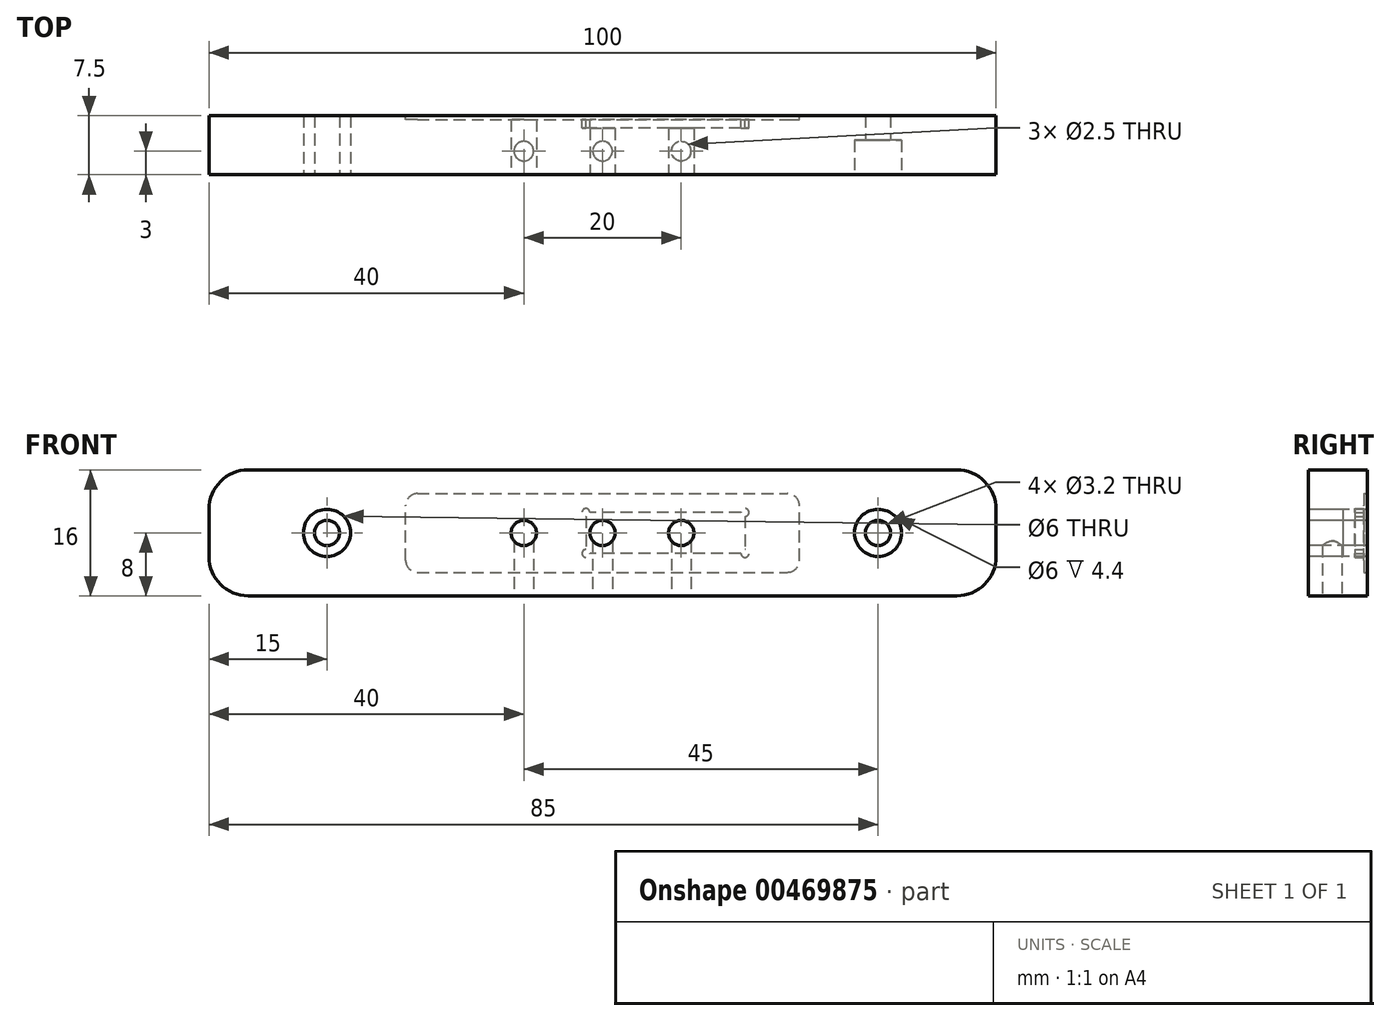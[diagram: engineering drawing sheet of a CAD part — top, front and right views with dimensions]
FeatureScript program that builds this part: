
annotation { "Feature Type Name" : "Feature", "Feature Type Description" : "" }
export const myFeature = defineFeature(function(context is Context, id is Id, definition is map)
    precondition{}
    {
        {
            var Q0;
            Q0=qCreatedBy(makeId("Front.planeOp"),FACE);
            var sketch = newSketch(context, id + "F0", { "sketchPlane" : qUnion([Q0])});
            skLineSegment(sketch, "E0.bottom", {"start": v(50, 8) * mm, "end": v(-50, 8) * mm});
            skLineSegment(sketch, "E0.top", {"start": v(50, -8) * mm, "end": v(-50, -8) * mm});
            skLineSegment(sketch, "E0.left", {"start": v(50, 8) * mm, "end": v(50, -8) * mm});
            skLineSegment(sketch, "E0.right", {"start": v(-50, 8) * mm, "end": v(-50, -8) * mm});
            skPoint(sketch, "E0.middle", {"position": v(0, 0) * mm});
            skSolve(sketch);
        }
        {
            var Q0;
            Q0=makeQuery(id+"F0.imprint","IMPRINT",FACE,{"disambiguationData":[TD([[makeQuery(id+"F0.imprint","IMPRINT",EDGE,{"derivedFrom":sQuery(id+"F0.wireOp",EDGE,"E0.bottom")}),1.0]])]});
            extrude(context, id + "F1", {"entities" : qUnion([Q0]), "depth" : 7.5 * mm});
        }
        {
            var Q0;
            Q0=makeQuery(id+"F1.opExtrude","CAP_FACE",FACE,{"disambiguationData":[OSD([sQuery(id+"F0.wireOp",EDGE,"E0.bottom"),sQuery(id+"F0.wireOp",EDGE,"E0.top"),sQuery(id+"F0.wireOp",EDGE,"E0.left"),sQuery(id+"F0.wireOp",EDGE,"E0.right")])],"isStart":false});
            var sketch = newSketch(context, id + "F2", { "sketchPlane" : qUnion([Q0])});
            skCircle(sketch, "E1", {"center": v(35, 0) * mm, "radius": 3 * mm});
            skCircle(sketch, "E2", {"center": v(35, 0) * mm, "radius": 1.6 * mm});
            skCircle(sketch, "E3.MirrorC", {"center": v(-35, 0) * mm, "radius": 1.6 * mm});
            skCircle(sketch, "E4.MirrorC", {"center": v(-35, 0) * mm, "radius": 3 * mm});
            skSolve(sketch);
        }
        {
            var Q0;
            Q0=makeQuery(id+"F2.imprint","IMPRINT",FACE,{"disambiguationData":[TD([[makeQuery(id+"F2.imprint","IMPRINT",EDGE,{"derivedFrom":sQuery(id+"F2.wireOp",EDGE,"E2")}),1.0]])]});
            var Q1;
            Q1=makeQuery(id+"F2.imprint","IMPRINT",FACE,{"disambiguationData":[TD([[makeQuery(id+"F2.imprint","IMPRINT",EDGE,{"derivedFrom":sQuery(id+"F2.wireOp",EDGE,"E3.MirrorC")}),-1.0]])]});
            extrude(context, id + "F3", {"entities" : qUnion([Q0, Q1]), "operationType" : NewBodyOperationType.REMOVE, "endBound" : BoundingType.THROUGH_ALL, "oppositeDirection" : true, "depth" : 25 * mm});
        }
        {
            var Q0;
            Q0 = qSketchRegion(id + "F2", true);
            extrude(context, id + "F4", {"entities" : qUnion([Q0]), "operationType" : NewBodyOperationType.REMOVE, "oppositeDirection" : true, "depth" : 4.4 * mm});
        }
        {
            var Q0;
            Q0=makeQuery(id+"F1.opExtrude","CAP_FACE",FACE,{"disambiguationData":[OSD([sQuery(id+"F0.wireOp",EDGE,"E0.bottom"),sQuery(id+"F0.wireOp",EDGE,"E0.top"),sQuery(id+"F0.wireOp",EDGE,"E0.left"),sQuery(id+"F0.wireOp",EDGE,"E0.right")])],"isStart":false});
            var sketch = newSketch(context, id + "F5", { "sketchPlane" : qUnion([Q0])});
            skCircle(sketch, "E5", {"center": v(10, 0) * mm, "radius": 1.6 * mm});
            skCircle(sketch, "E6.MirrorC", {"center": v(-10, 0) * mm, "radius": 1.6 * mm});
            skCircle(sketch, "E7", {"center": v(0, 0) * mm, "radius": 1.6 * mm});
            skSolve(sketch);
        }
        {
            var Q0;
            Q0=makeQuery(id+"F5.imprint","IMPRINT",FACE,{"disambiguationData":[TD([[makeQuery(id+"F5.imprint","IMPRINT",EDGE,{"derivedFrom":sQuery(id+"F5.wireOp",EDGE,"E5")}),1.0]])]});
            var Q1;
            Q1=makeQuery(id+"F5.imprint","IMPRINT",FACE,{"disambiguationData":[TD([[makeQuery(id+"F5.imprint","IMPRINT",EDGE,{"derivedFrom":sQuery(id+"F5.wireOp",EDGE,"E6.MirrorC")}),-1.0]])]});
            extrude(context, id + "F6", {"entities" : qUnion([Q0, Q1]), "operationType" : NewBodyOperationType.REMOVE, "endBound" : BoundingType.THROUGH_ALL, "oppositeDirection" : true, "depth" : 25 * mm});
        }
        {
            var Q0;
            Q0=makeQuery(id+"F1.opExtrude","CAP_FACE",FACE,{"disambiguationData":[OSD([sQuery(id+"F0.wireOp",EDGE,"E0.bottom"),sQuery(id+"F0.wireOp",EDGE,"E0.top"),sQuery(id+"F0.wireOp",EDGE,"E0.left"),sQuery(id+"F0.wireOp",EDGE,"E0.right")])],"isStart":true});
            var sketch = newSketch(context, id + "F7", { "sketchPlane" : qUnion([Q0])});
            skLineSegment(sketch, "E8.bottom", {"start": v(25, -5) * mm, "end": v(-25, -5) * mm});
            skLineSegment(sketch, "E8.top", {"start": v(25, 5) * mm, "end": v(-25, 5) * mm});
            skLineSegment(sketch, "E8.left", {"start": v(25, -5) * mm, "end": v(25, 5) * mm});
            skLineSegment(sketch, "E8.right", {"start": v(-25, -5) * mm, "end": v(-25, 5) * mm});
            skPoint(sketch, "E8.middle", {"position": v(0, 0) * mm});
            skLineSegment(sketch, "E9.bottom", {"start": v(-17.6, 2.6) * mm, "end": v(1.6, 2.6) * mm});
            skLineSegment(sketch, "E9.top", {"start": v(-17.6, -2.6) * mm, "end": v(1.6, -2.6) * mm});
            skLineSegment(sketch, "E9.left", {"start": v(-18.1, 2.1) * mm, "end": v(-18.1, -2.1) * mm});
            skLineSegment(sketch, "E9.right", {"start": v(2.1, 2.1) * mm, "end": v(2.1, -2.1) * mm});
            skArc(sketch, "E10", {"start": v(-17.6, 2.6) * mm, "mid": v(-18.45, 2.95) * mm, "end": v(-18.1, 2.1) * mm});
            skArc(sketch, "E11.MirrorC", {"start": v(-17.6, -2.6) * mm, "mid": v(-18.45, -2.95) * mm, "end": v(-18.1, -2.1) * mm});
            skArc(sketch, "E12.MirrorC", {"start": v(1.6, 2.6) * mm, "mid": v(2.45, 2.95) * mm, "end": v(2.1, 2.1) * mm});
            skArc(sketch, "E13.MirrorC", {"start": v(1.6, -2.6) * mm, "mid": v(2.45, -2.95) * mm, "end": v(2.1, -2.1) * mm});
            skSolve(sketch);
        }
        {
            var Q0;
            Q0=makeQuery(id+"F7.imprint","IMPRINT",FACE,{"disambiguationData":[TD([[makeQuery(id+"F7.imprint","IMPRINT",EDGE,{"derivedFrom":sQuery(id+"F7.wireOp",EDGE,"E8.bottom")}),-1.0]])]});
            extrude(context, id + "F8", {"entities" : qUnion([Q0]), "operationType" : NewBodyOperationType.REMOVE, "oppositeDirection" : true, "depth" : .5 * mm});
        }
        {
            var Q0;
            Q0=makeQuery(id+"F8.boolean.opBoolean","SPLIT",FACE,{"disambiguationData":[TD([makeQuery(id+"F6.boolean.opBoolean","COPY",FACE,{"derivedFrom":makeQuery(id+"F6.opExtrude","SWEPT_FACE",FACE,{"disambiguationData":[OSD([sQuery(id+"F5.wireOp",EDGE,"E5")])]})})])],"derivedFrom":makeQuery(id+"F1.opExtrude","CAP_FACE",FACE,{"disambiguationData":[OSD([sQuery(id+"F0.wireOp",EDGE,"E0.bottom"),sQuery(id+"F0.wireOp",EDGE,"E0.top"),sQuery(id+"F0.wireOp",EDGE,"E0.left"),sQuery(id+"F0.wireOp",EDGE,"E0.right")])],"isStart":true})});
            extrude(context, id + "F9", {"entities" : qUnion([Q0]), "operationType" : NewBodyOperationType.REMOVE, "oppositeDirection" : true, "depth" : 1.6 * mm});
        }
        {
            var Q0;
            Q0=makeQuery(id+"F8.boolean.opBoolean","COPY",EDGE,{"derivedFrom":makeQuery(id+"F8.opExtrude","SWEPT_EDGE",EDGE,{"disambiguationData":[OSD([sQuery(id+"F7.wireOp",EDGE,"E8.top"),sQuery(id+"F7.wireOp",EDGE,"E8.left")])]})});
            var Q1;
            Q1=makeQuery(id+"F8.boolean.opBoolean","COPY",EDGE,{"derivedFrom":makeQuery(id+"F8.opExtrude","SWEPT_EDGE",EDGE,{"disambiguationData":[OSD([sQuery(id+"F7.wireOp",EDGE,"E8.bottom"),sQuery(id+"F7.wireOp",EDGE,"E8.left")])]})});
            var Q2;
            Q2=makeQuery(id+"F8.boolean.opBoolean","COPY",EDGE,{"derivedFrom":makeQuery(id+"F8.opExtrude","SWEPT_EDGE",EDGE,{"disambiguationData":[OSD([sQuery(id+"F7.wireOp",EDGE,"E8.bottom"),sQuery(id+"F7.wireOp",EDGE,"E8.right")])]})});
            var Q3;
            Q3=makeQuery(id+"F8.boolean.opBoolean","COPY",EDGE,{"derivedFrom":makeQuery(id+"F8.opExtrude","SWEPT_EDGE",EDGE,{"disambiguationData":[OSD([sQuery(id+"F7.wireOp",EDGE,"E8.top"),sQuery(id+"F7.wireOp",EDGE,"E8.right")])]})});
            fillet(context, id + "F10", {"entities" : qUnion([Q0, Q1, Q2, Q3]), "radius" : 1.5 * mm, "tangentPropagation" : true, "allowEdgeOverflow" : false});
        }
        {
            var Q0;
            Q0=makeQuery(id+"F1.opExtrude","SWEPT_FACE",FACE,{"disambiguationData":[OSD([sQuery(id+"F0.wireOp",EDGE,"E0.top")])]});
            var sketch = newSketch(context, id + "F11", { "sketchPlane" : qUnion([Q0])});
            skCircle(sketch, "E14", {"center": v(10, 4.5) * mm, "radius": 1.25 * mm});
            skCircle(sketch, "E15", {"center": v(0, 4.5) * mm, "radius": 1.25 * mm});
            skCircle(sketch, "E16.MirrorC", {"center": v(-10, 4.5) * mm, "radius": 1.25 * mm});
            skSolve(sketch);
        }
        {
            var Q0;
            Q0=makeQuery(id+"F11.imprint","IMPRINT",FACE,{"disambiguationData":[TD([[makeQuery(id+"F11.imprint","IMPRINT",EDGE,{"derivedFrom":sQuery(id+"F11.wireOp",EDGE,"E14")}),1.0]])]});
            var Q1;
            Q1=makeQuery(id+"F11.imprint","IMPRINT",FACE,{"disambiguationData":[TD([[makeQuery(id+"F11.imprint","IMPRINT",EDGE,{"derivedFrom":sQuery(id+"F11.wireOp",EDGE,"E15")}),1.0]])]});
            extrude(context, id + "F12", {"entities" : qUnion([Q0, Q1]), "operationType" : NewBodyOperationType.REMOVE, "oppositeDirection" : true, "depth" : 8 * mm});
        }
        {
            var Q0;
            Q0=makeQuery(id+"F1.opExtrude","SWEPT_EDGE",EDGE,{"disambiguationData":[OSD([sQuery(id+"F0.wireOp",EDGE,"E0.bottom"),sQuery(id+"F0.wireOp",EDGE,"E0.right")])]});
            var Q1;
            Q1=makeQuery(id+"F1.opExtrude","SWEPT_EDGE",EDGE,{"disambiguationData":[OSD([sQuery(id+"F0.wireOp",EDGE,"E0.top"),sQuery(id+"F0.wireOp",EDGE,"E0.right")])]});
            var Q2;
            Q2=makeQuery(id+"F1.opExtrude","SWEPT_EDGE",EDGE,{"disambiguationData":[OSD([sQuery(id+"F0.wireOp",EDGE,"E0.bottom"),sQuery(id+"F0.wireOp",EDGE,"E0.left")])]});
            var Q3;
            Q3=makeQuery(id+"F1.opExtrude","SWEPT_EDGE",EDGE,{"disambiguationData":[OSD([sQuery(id+"F0.wireOp",EDGE,"E0.top"),sQuery(id+"F0.wireOp",EDGE,"E0.left")])]});
            fillet(context, id + "F13", {"entities" : qUnion([Q0, Q1, Q2, Q3]), "radius" : 5 * mm, "tangentPropagation" : true, "allowEdgeOverflow" : false});
        }
        {
            var Q0;
            Q0 = qSketchRegion(id + "F11", true);
            extrude(context, id + "F14", {"entities" : qUnion([Q0]), "operationType" : NewBodyOperationType.REMOVE, "oppositeDirection" : true, "depth" : 8 * mm});
        }
        {
            var Q0;
            Q0 = qSketchRegion(id + "F5", true);
            extrude(context, id + "F15", {"entities" : qUnion([Q0]), "operationType" : NewBodyOperationType.REMOVE, "endBound" : BoundingType.THROUGH_ALL, "oppositeDirection" : true, "depth" : 25 * mm});
        }
    });
